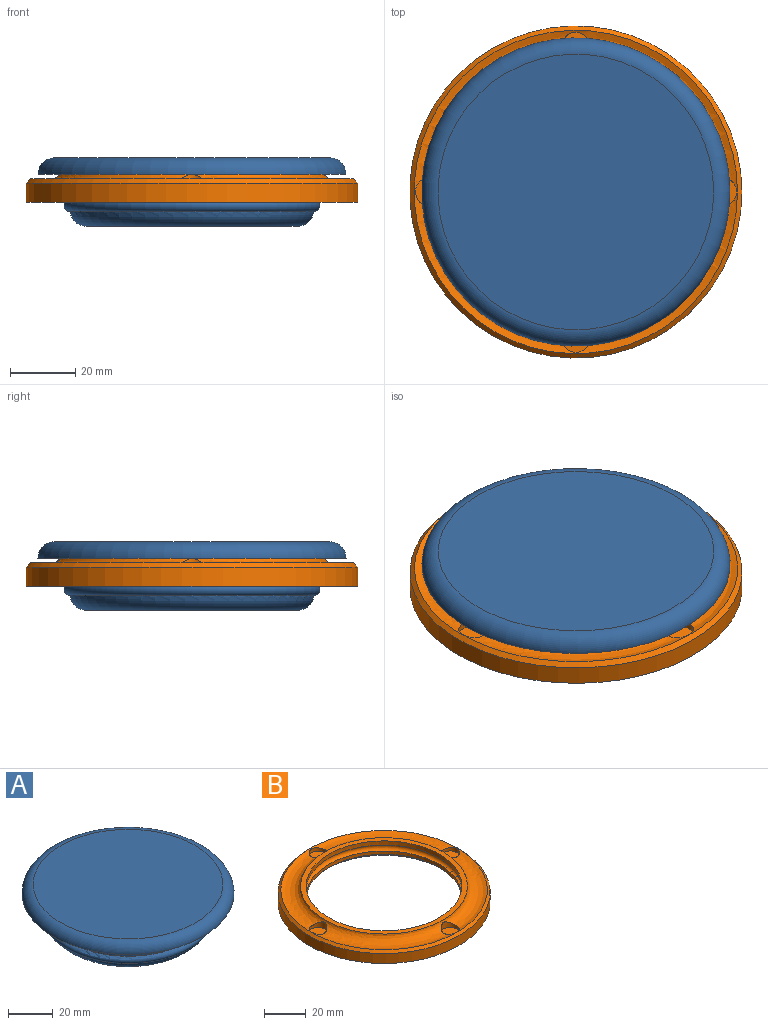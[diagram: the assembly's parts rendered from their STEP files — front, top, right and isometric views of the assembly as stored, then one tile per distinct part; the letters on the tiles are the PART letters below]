
ASSEMBLY  parts=2 mates=1
PART A: 12 faces, bbox 102.5x102.5x21 mm
  f0: plane 64.93x64.93mm, normal (0,0,-1), area 86.2mm2, adj f3,f4
  f1: cylinder r=27.04mm len=54.08mm, axis (0,0,-1), area 713.6mm2, adj f2,f3
  f2: plane 54.08x54.08mm, normal (0,0,-1), area 2296.9mm2, adj f1
  f3: torus R=32.04mm, axis (0,0,1), area 1424mm2, adj f0,f1
  f4: torus R=32.47mm, axis (0,0,1), area 1653.7mm2, adj f0,f5
  f5: torus R=37.5mm, axis (0,0,1), area 1358.8mm2, adj f4,f6
  f6: cylinder r=37.46mm len=74.93mm, axis (0,0,-1), area 454.6mm2, adj f5,f7
  f7: torus R=37.5mm, axis (0,0,1), area 1354.1mm2, adj f6,f11
  f8: plane 84.66x84.66mm, normal (0,0,1), area 5629mm2, adj f9
  f9: torus R=42.33mm, axis (0,0,1), area 2245.9mm2, adj f8,f10
  f10: plane 94.66x94.66mm, normal (0,0,-1), area 2627.7mm2, adj f9,f11
  f11: cylinder r=37.46mm len=74.93mm, axis (0,0,-1), area 588.2mm2, adj f7,f10
PART B: 17 faces, bbox 102x102x10.9 mm
  f0: cylinder r=37.46mm len=74.93mm, axis (0,0,1), area 578.7mm2, adj f1,f15
  f1: plane 80.27x80.27mm, normal (0,0,1), area 650.6mm2, adj f0,f5
  f2: cylinder r=51mm len=102mm, axis (0,0,-1), area 1872mm2, adj f3,f4
  f3: plane 102x102mm, normal (0,0,-1), area 3356.5mm2, adj f2,f14
  f4: cone r=47.19mm half-angle=45deg, axis (0,0,-1), area 603.6mm2, adj f2,f5
  f5: bspline ~98.8x98.42mm, area 2829.9mm2, adj f1,f4,f6,f8,f10,f12
  f6: cylinder r=4.33mm len=8.66mm, axis (0,0,1), area 64.4mm2, adj f5,f7
  f7: plane 8.66x8.66mm, normal (0,0,1), area 58.9mm2, adj f6
  f8: cylinder r=4.33mm len=8.66mm, axis (0,0,1), area 64.5mm2, adj f5,f9
  f9: plane 8.66x8.66mm, normal (0,0,1), area 58.9mm2, adj f8
  f10: cylinder r=4.33mm len=8.66mm, axis (0,0,1), area 65.7mm2, adj f5,f11
  f11: plane 8.66x8.66mm, normal (0,0,1), area 58.9mm2, adj f10
  f12: cylinder r=4.33mm len=8.66mm, axis (0,0,1), area 63.8mm2, adj f5,f13
  f13: plane 8.66x8.66mm, normal (0,0,1), area 58.9mm2, adj f12
  f14: torus R=37.39mm, axis (0,0,-1), area 650.2mm2, adj f3,f16
  f15: torus R=37.39mm, axis (0,0,-1), area 1300.4mm2, adj f0,f16
  f16: cylinder r=37.46mm len=74.93mm, axis (0,0,1), area 455.1mm2, adj f14,f15
PLACE A t=(25.55,3.71,-7.37)mm
PLACE B t=(25.55,3.71,0)mm
MATE slider A.f9 <-> B.f2  axis (0,0,1) through (25.55,3.71,12.16)mm
